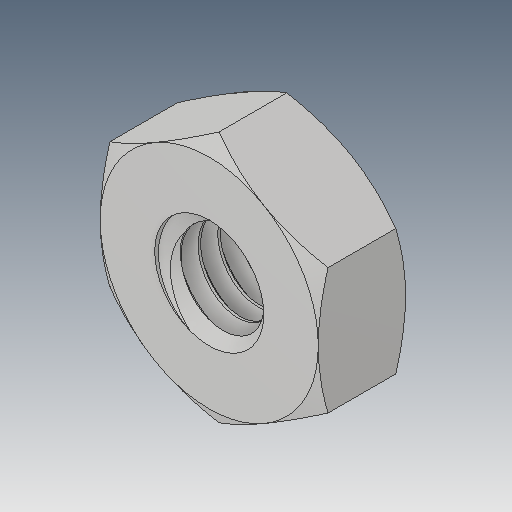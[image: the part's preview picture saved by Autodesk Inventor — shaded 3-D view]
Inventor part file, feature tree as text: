
AUTODESK INVENTOR PART (.ipt)
format: ipt  version: 2018 (Build 220112000, 112)  size: 281,600 bytes
history: native  units: mm
features: mirror x1
ambient origin geometry x8: Origin, YZ Plane, XZ Plane, XY Plane, X Axis, Y Axis, Z Axis, Center Point
bodies: Solid1 (feature_tree)
feature tree (1):
  mirror  "Mirror2"
